# Revit family: AFX-Harper-LED_Vanity-1
name_source: partatom
category: Lighting Fixtures
units: mm (PartAtom-declared; Revit-internal decimal feet)

## family parameters
Cut with Voids When Loaded = No
Host = Face
Light Source = Yes
Part Type = Normal
Room Calculation Point = No
Round Connector Dimension = Use Diameter
Shared = No

## types (10) — shared parameters
Apparent Load = 120 VA
Assembly Code = D5020200
Body Finish = AFX - Aluminum Black
Cable Finish = AFX - Aluminum Black
Canopy Finish = AFX - Aluminum Black
Cap Finish = AFX - Aluminum Black
Color Filter = 16777215
Color Rendering Index = 90
Colour Rendering Index = 90 CRI
Default Elevation = 48"
Depth = 3 3/4"
Diffuser Finish = AFX - White Acrylic
Dimming Lamp Color Temperature Shift = <None>
Emit Shape Visible in Rendering = No
Emit from Rectangle Length = 48"
Emit from Rectangle Width = 24"
Height = 4 1/2"
Lamp = LED
Manufacturer = AFX Inc
Product Documentation Link = https://www.afxinc.com
Revit Model Built By = https://servex-us.com
Support Finish = AFX - Aluminum Black
Tilt Angle = 90.00°
Type Comments = Harper
URL = https://www.afxinc.com
Voltage = 120 V
Wattage Comments = 40W

## per-type parameters (varying)
| type | 24L | 36L | Description | Length | Photometric Web File |
| HPRV2405LAJUDBK-2700K | Yes | No | 24'' LED Vanity - 2700K - 24 3/4"L x 4 1/2"H x 3 3/4"D | 24 3/4" | HPRV2405LAJUDSN SB BK_2700K IES.IES |
| HPRV2405LAJUDBK-3000K | Yes | No | 24'' LED Vanity - 3000K - 24 3/4"L x 4 1/2"H x 3 3/4"D | 24 3/4" | HPRV2405LAJUDSN SB BK_3000K IES.IES |
| HPRV2405LAJUDBK-3500K | Yes | No | 24'' LED Vanity - 3500K - 24 3/4"L x 4 1/2"H x 3 3/4"D | 24 3/4" | HPRV2405LAJUDSN SB BK_3500K IES.IES |
| HPRV2405LAJUDBK-4000K | Yes | No | 24'' LED Vanity - 4000K - 24 3/4"L x 4 1/2"H x 3 3/4"D | 24 3/4" | HPRV2405LAJUDSN SB BK_4000K IES.IES |
| HPRV2405LAJUDBK-5000K | Yes | No | 24'' LED Vanity - 5000K - 24 3/4"L x 4 1/2"H x 3 3/4"D | 24 3/4" | HPRV2405LAJUDSN SB BK_5000K IES.IES |
| HPRV3605LAJUDBK-2700K | No | Yes | 36'' LED Vanity - 2700K - 36 3/8"L x 4 1/2"H x 3 3/4"D | 36 3/8" | HPRV3605LAJUDSN SB BK_2700K IES.IES |
| HPRV3605LAJUDBK-3000K | No | Yes | 36'' LED Vanity - 3000K - 36 3/8"L x 4 1/2"H x 3 3/4"D | 36 3/8" | HPRV3605LAJUDSN SB BK_3000K IES.IES |
| HPRV3605LAJUDBK-3500K | No | Yes | 36'' LED Vanity - 3500K - 36 3/8"L x 4 1/2"H x 3 3/4"D | 36 3/8" | HPRV3605LAJUDSN SB BK_3500K IES.IES |
| HPRV3605LAJUDBK-4000K | No | Yes | 36'' LED Vanity - 4000K - 36 3/8"L x 4 1/2"H x 3 3/4"D | 36 3/8" | HPRV3605LAJUDSN SB BK_4000K IES.IES |
| HPRV3605LAJUDBK-5000K | No | Yes | 36'' LED Vanity - 5000K - 36 3/8"L x 4 1/2"H x 3 3/4"D | 36 3/8" | HPRV3605LAJUDSN SB BK_5000K IES.IES |

note: column(s) folded — value = type name in every type: Model

## geometry (parser evidence)
native form markers: Sweep x8
no freeform markers — native parametric forms only
